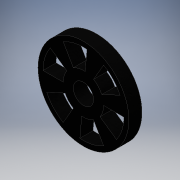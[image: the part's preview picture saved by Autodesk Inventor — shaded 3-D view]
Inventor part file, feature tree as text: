
AUTODESK INVENTOR PART (.ipt)
format: ipt  version: 2016 (Build 200138000, 138)  size: 136,192 bytes
history: native  units: mm
features: extrude x2, sketch x2, pattern_circular x1
ambient origin geometry x8: Origin, YZ Plane, XZ Plane, XY Plane, X Axis, Y Axis, Z Axis, Center Point
bodies: Solid1 (feature_tree)
feature tree (5):
  extrude  "Extrusion1"  Depth=13.0mm TaperAngle=0.0deg
  extrude  "Extrusion2"  Depth=40.0mm
  pattern_circular  "Circular Pattern1"  [2 undecoded]
  sketch  "Sketch1"  dims[d0=90.0mm d1=13.0mm d2=0.0mm]
  sketch  "Sketch2"  dims[d3=20.0mm d5=6.108652mm d10=13.0mm d11=0.0mm d12=60.0mm d13=360.0deg d16=40.0mm]
note: 2 required parameter values undecoded (feature->parameter linkage not recoverable at this tier; creation-order binding heuristic only, values carry confidence <= 0.55)
